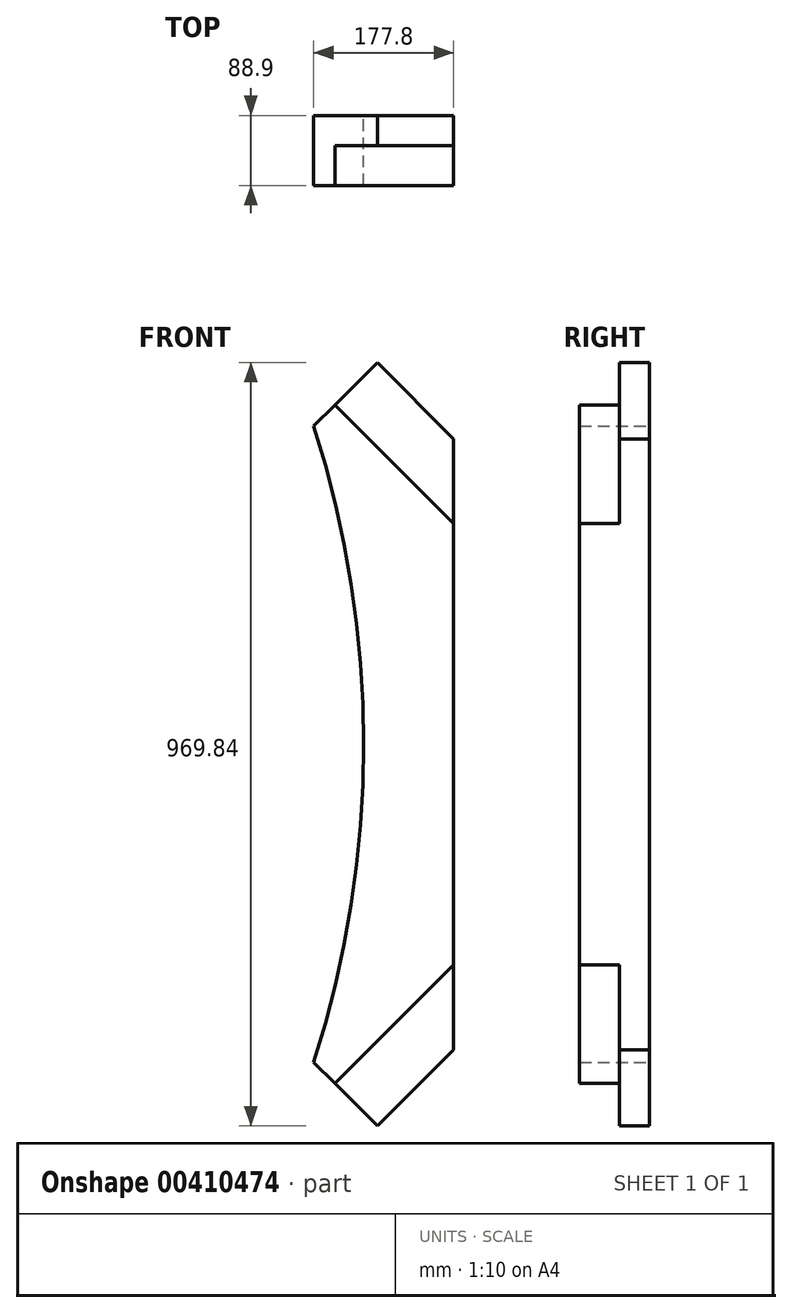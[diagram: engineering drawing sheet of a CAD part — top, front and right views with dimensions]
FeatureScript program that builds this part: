
annotation { "Feature Type Name" : "Feature", "Feature Type Description" : "" }
export const myFeature = defineFeature(function(context is Context, id is Id, definition is map)
    precondition{}
    {
        {
            var Q0;
            Q0=qCreatedBy(makeId("Front.planeOp"),FACE);
            var sketch = newSketch(context, id + "F0", { "sketchPlane" : qUnion([Q0])});
            skLineSegment(sketch, "E0.bottom", {"start": v(-88.9, 698.5) * mm, "end": v(88.9, 698.5) * mm});
            skLineSegment(sketch, "E0.top", {"start": v(-88.9, -698.5) * mm, "end": v(88.9, -698.5) * mm});
            skLineSegment(sketch, "E0.left", {"start": v(-88.9, 698.5) * mm, "end": v(-88.9, -698.5) * mm});
            skLineSegment(sketch, "E0.right", {"start": v(88.9, 698.5) * mm, "end": v(88.9, -698.5) * mm});
            skPoint(sketch, "E0.middle", {"position": v(0, 0) * mm});
            skLineSegment(sketch, "E1", {"start": v(-88.9, 543.35) * mm, "end": v(88.9, 365.55) * mm});
            skLineSegment(sketch, "E2", {"start": v(-88.9, 543.35) * mm, "end": v(-8.08, 624.17) * mm});
            skLineSegment(sketch, "E3", {"start": v(-8.08, 624.17) * mm, "end": v(88.9, 527.2) * mm});
            skLineSegment(sketch, "E4", {"start": v(-61.96, 570.3) * mm, "end": v(88.9, 419.43) * mm});
            skLineSegment(sketch, "E5", {"start": v(88.9, -87.04) * mm, "end": v(-88.9, -264.84) * mm});
            skLineSegment(sketch, "E6", {"start": v(-88.9, -264.84) * mm, "end": v(-8.08, -345.67) * mm});
            skLineSegment(sketch, "E7", {"start": v(-8.08, -345.67) * mm, "end": v(88.9, -248.69) * mm});
            skLineSegment(sketch, "E8", {"start": v(88.9, -140.93) * mm, "end": v(-61.96, -291.78) * mm});
            skArc(sketch, "E9", {"start": v(-88.9, -264.84) * mm, "mid": v(-25.4, 139.25) * mm, "end": v(-88.9, 543.35) * mm});
            skSolve(sketch);
        }
        {
            var Q0;
            {var subQ0=sQuery(id+"F0.wireOp",EDGE,"E1");Q0=makeQuery(id+"F0.imprint","IMPRINT",FACE,{"disambiguationData":[TD([[makeQuery(id+"F0.imprint","IMPRINT",EDGE,{"derivedFrom":subQ0}),-1.0]])]});}
            var Q1;
            {var subQ0=sQuery(id+"F0.wireOp",EDGE,"E5");Q1=makeQuery(id+"F0.imprint","IMPRINT",FACE,{"disambiguationData":[TD([[makeQuery(id+"F0.imprint","IMPRINT",EDGE,{"derivedFrom":subQ0}),1.0]])]});}
            var Q2;
            {var subQ0=sQuery(id+"F0.wireOp",EDGE,"E1");Q2=makeQuery(id+"F0.imprint","IMPRINT",FACE,{"disambiguationData":[TD([[makeQuery(id+"F0.imprint","IMPRINT",EDGE,{"derivedFrom":subQ0}),1.0]])]});}
            extrude(context, id + "F1", {"entities" : qUnion([Q0, Q1, Q2]), "depth" : 88.9 * mm});
        }
        {
            var Q0;
            {var subQ0=sQuery(id+"F0.wireOp",EDGE,"E3");Q0=makeQuery(id+"F0.imprint","IMPRINT",FACE,{"disambiguationData":[TD([[makeQuery(id+"F0.imprint","IMPRINT",EDGE,{"derivedFrom":subQ0}),-1.0]])]});}
            var Q1;
            {var subQ0=sQuery(id+"F0.wireOp",EDGE,"E7");Q1=makeQuery(id+"F0.imprint","IMPRINT",FACE,{"disambiguationData":[TD([[makeQuery(id+"F0.imprint","IMPRINT",EDGE,{"derivedFrom":subQ0}),1.0]])]});}
            extrude(context, id + "F2", {"entities" : qUnion([Q0, Q1]), "operationType" : NewBodyOperationType.ADD, "depth" : 38.1 * mm});
        }
    });
